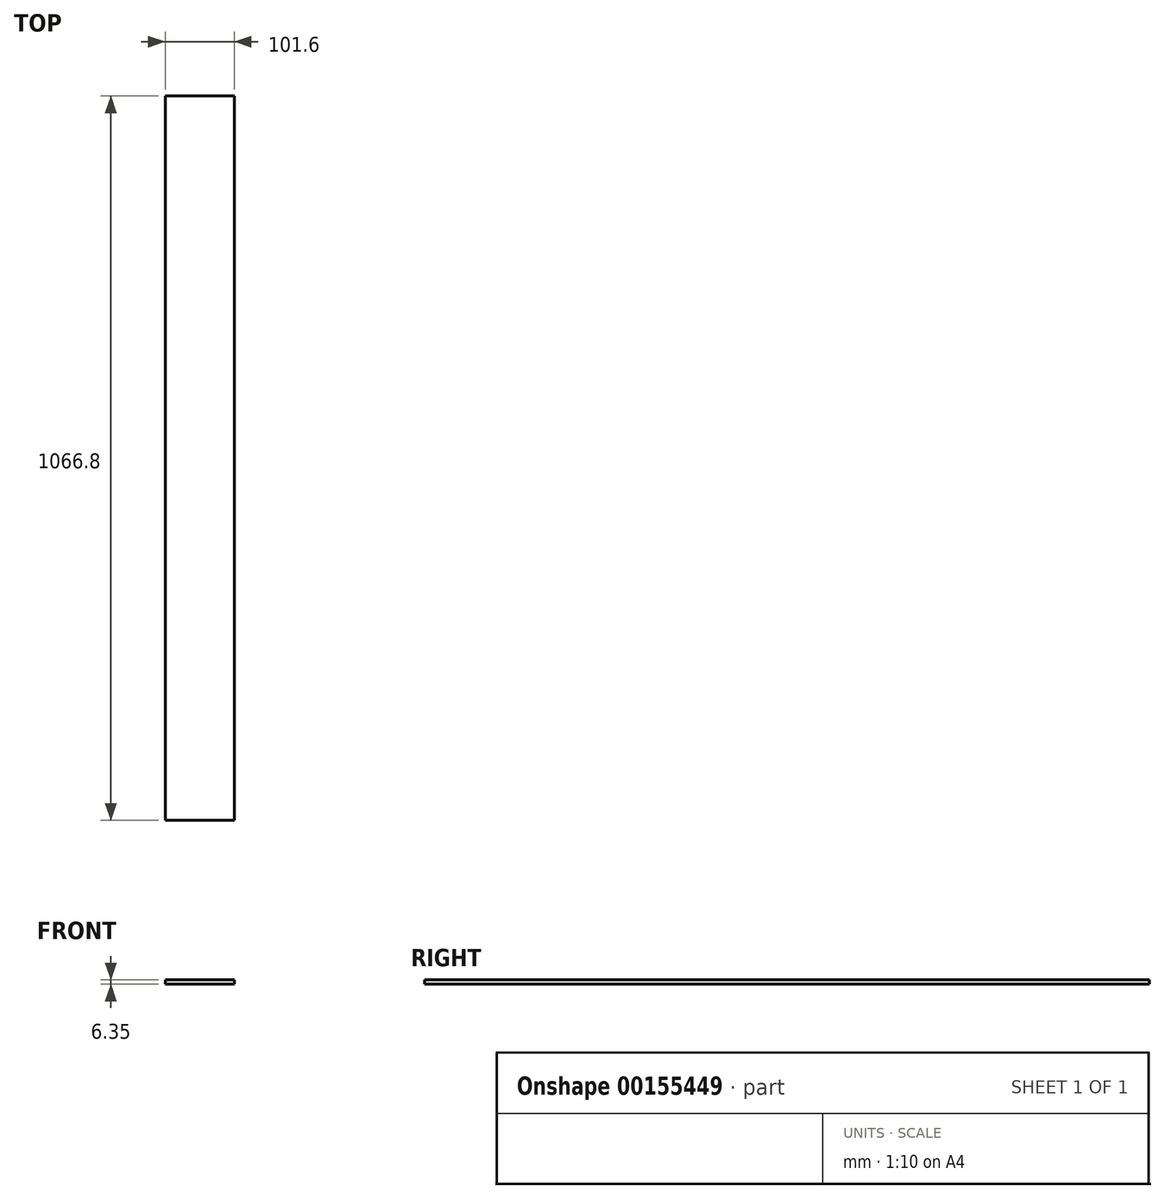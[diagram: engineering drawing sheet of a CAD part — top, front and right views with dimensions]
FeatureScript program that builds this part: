
annotation { "Feature Type Name" : "Feature", "Feature Type Description" : "" }
export const myFeature = defineFeature(function(context is Context, id is Id, definition is map)
    precondition{}
    {
        {
            var Q0;
            Q0=qCreatedBy(makeId("Top.planeOp"),FACE);
            var sketch = newSketch(context, id + "F0", { "sketchPlane" : qUnion([Q0])});
            skLineSegment(sketch, "E0.bottom", {"start": v(0, 0) * mm, "end": v(101.6, 0) * mm});
            skLineSegment(sketch, "E0.top", {"start": v(0, 1066.8) * mm, "end": v(101.6, 1066.8) * mm});
            skLineSegment(sketch, "E0.left", {"start": v(0, 0) * mm, "end": v(0, 1066.8) * mm});
            skLineSegment(sketch, "E0.right", {"start": v(101.6, 0) * mm, "end": v(101.6, 1066.8) * mm});
            skSolve(sketch);
        }
        {
            var Q0;
            Q0 = qSketchRegion(id + "F0", true);
            extrude(context, id + "F1", {"entities" : qUnion([Q0]), "depth" : 6.35 * mm});
        }
    });
